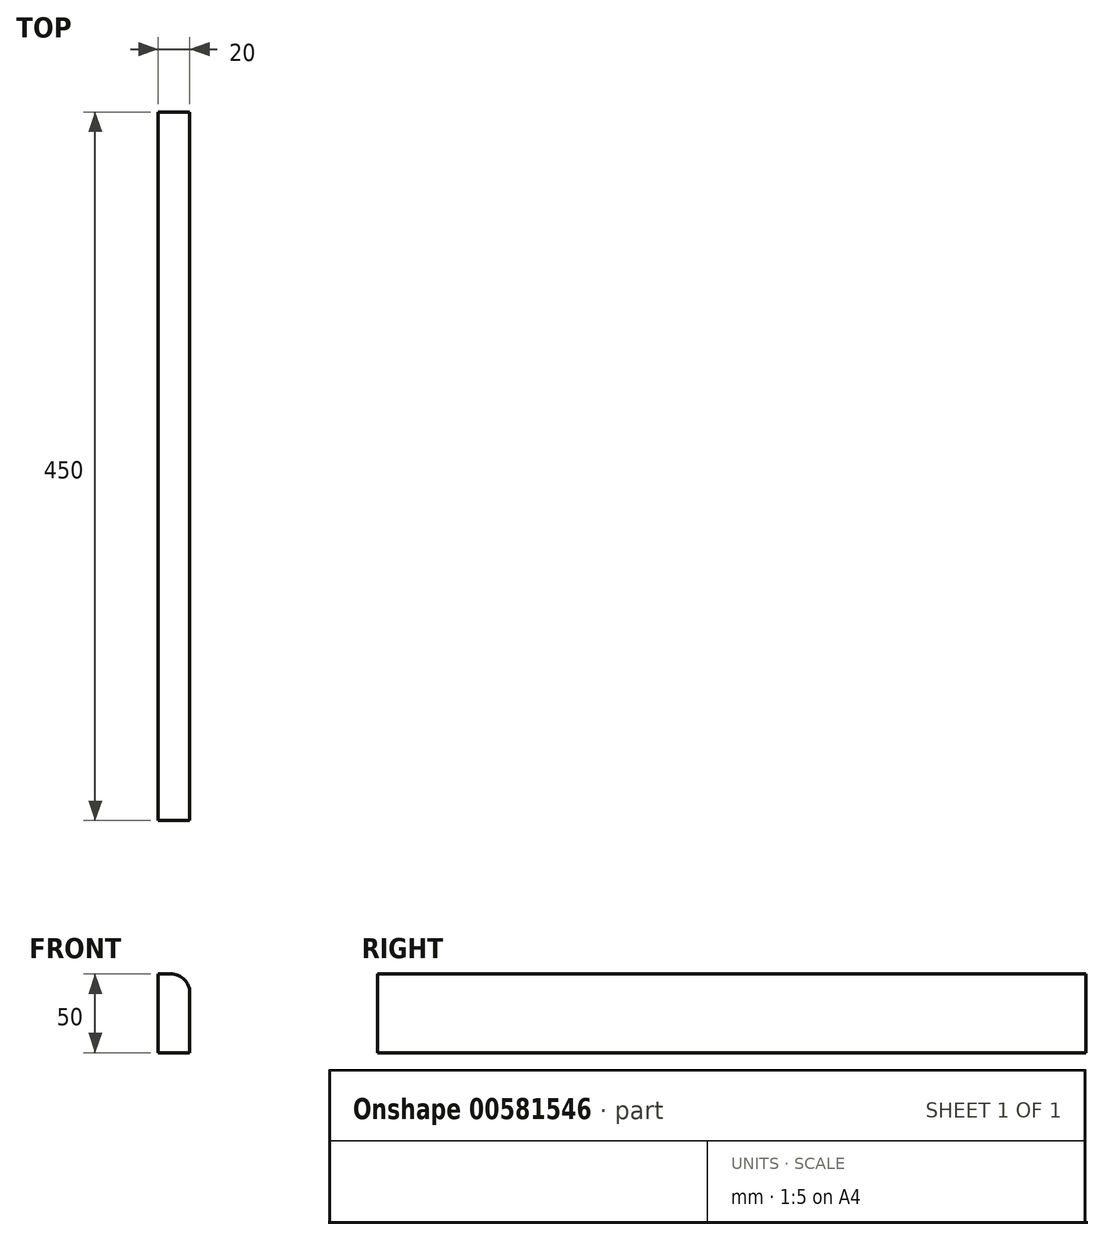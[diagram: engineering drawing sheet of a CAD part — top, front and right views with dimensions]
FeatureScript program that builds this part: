
annotation { "Feature Type Name" : "Feature", "Feature Type Description" : "" }
export const myFeature = defineFeature(function(context is Context, id is Id, definition is map)
    precondition{}
    {
        {
            var Q0;
            Q0=qCreatedBy(makeId("Top.planeOp"),FACE);
            var sketch = newSketch(context, id + "F0", { "sketchPlane" : qUnion([Q0])});
            skLineSegment(sketch, "E0.bottom", {"start": v(8.95, 433.5) * mm, "end": v(28.95, 433.5) * mm});
            skLineSegment(sketch, "E0.top", {"start": v(8.95, -16.5) * mm, "end": v(28.95, -16.5) * mm});
            skLineSegment(sketch, "E0.left", {"start": v(8.95, 433.5) * mm, "end": v(8.95, -16.5) * mm});
            skLineSegment(sketch, "E0.right", {"start": v(28.95, 433.5) * mm, "end": v(28.95, -16.5) * mm});
            skSolve(sketch);
        }
        {
            var Q0;
            Q0=makeQuery(id+"F0.imprint","IMPRINT",FACE,{"disambiguationData":[TD([[makeQuery(id+"F0.imprint","IMPRINT",EDGE,{"derivedFrom":sQuery(id+"F0.wireOp",EDGE,"E0.bottom")}),-1.0]])]});
            extrude(context, id + "F1", {"entities" : qUnion([Q0]), "depth" : 50 * mm, "offsetDistance" : 25 * mm});
        }
        {
            var Q0;
            Q0=makeQuery(id+"F1.opExtrude","CAP_EDGE",EDGE,{"disambiguationData":[OSD([sQuery(id+"F0.wireOp",EDGE,"E0.right")])],"isStart":false});
            fillet(context, id + "F2", {"entities" : qUnion([Q0]), "radius" : 12 * mm, "tangentPropagation" : true, "allowEdgeOverflow" : false});
        }
    });
